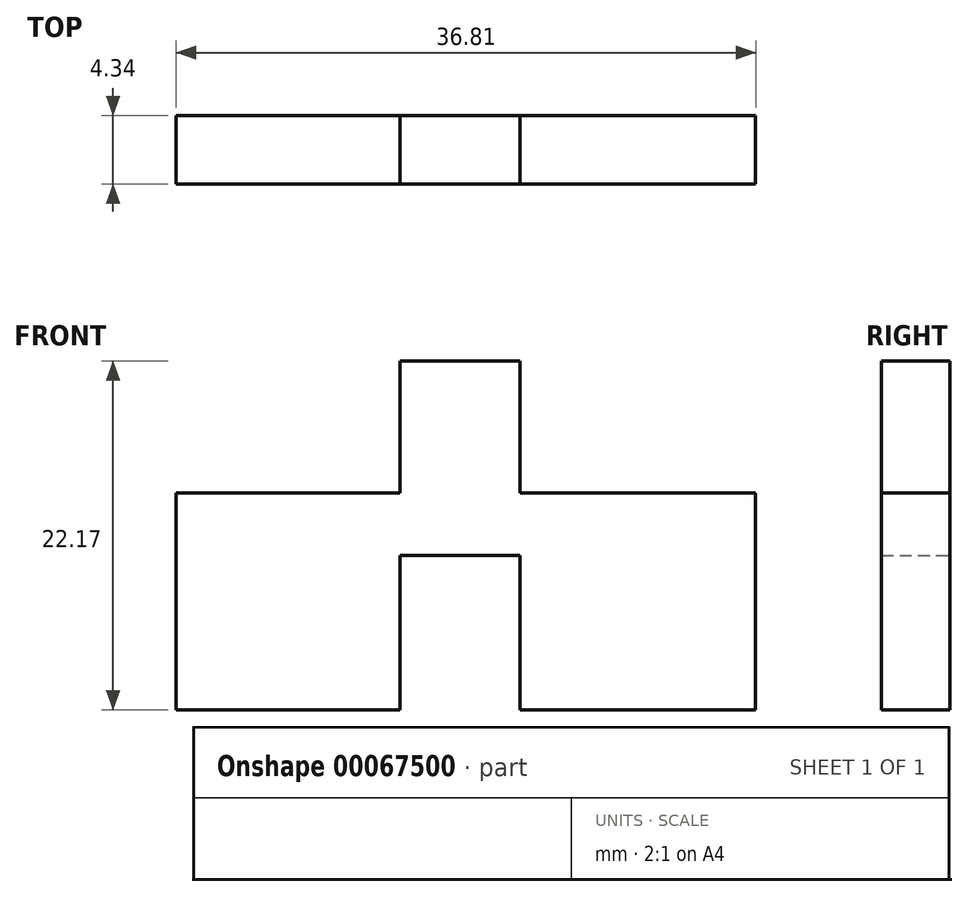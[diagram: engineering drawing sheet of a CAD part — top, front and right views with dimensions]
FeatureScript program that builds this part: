
annotation { "Feature Type Name" : "Feature", "Feature Type Description" : "" }
export const myFeature = defineFeature(function(context is Context, id is Id, definition is map)
    precondition{}
    {
        {
            var Q0;
            Q0=qCreatedBy(makeId("Front.planeOp"),FACE);
            var sketch = newSketch(context, id + "F0", { "sketchPlane" : qUnion([Q0])});
            skLineSegment(sketch, "E0.bottom", {"start": v(-23.81, 14.56) * mm, "end": v(-16.2, 14.56) * mm});
            skLineSegment(sketch, "E0.left", {"start": v(-38.04, 6.17) * mm, "end": v(-38.04, -4.28) * mm});
            skLineSegment(sketch, "E1.left", {"start": v(-23.81, 14.56) * mm, "end": v(-23.81, 6.17) * mm});
            skLineSegment(sketch, "E1.right", {"start": v(-16.2, 14.56) * mm, "end": v(-16.2, 6.17) * mm});
            skPoint(sketch, "E2.orphan", {"position": v(-12.63, 14.56) * mm});
            skPoint(sketch, "E3.orphan", {"position": v(-38.04, 14.56) * mm});
            skPoint(sketch, "E4.orphan", {"position": v(-25.33, 14.56) * mm});
            skPoint(sketch, "E5.end.orphan", {"position": v(-25.33, 0) * mm});
            skLineSegment(sketch, "E6", {"start": v(-38.04, -4.28) * mm, "end": v(-38.04, -7.61) * mm});
            skLineSegment(sketch, "E7.MirrorCS", {"start": v(-1.23, -4.28) * mm, "end": v(-1.23, -7.61) * mm});
            skPoint(sketch, "E8.end.orphan", {"position": v(-30.22, -0.18) * mm});
            skPoint(sketch, "E9.end.orphan", {"position": v(-30.22, -3.5) * mm});
            skLineSegment(sketch, "E10", {"start": v(-38.04, -7.61) * mm, "end": v(-23.81, -7.61) * mm});
            skLineSegment(sketch, "E11", {"start": v(-1.23, 6.17) * mm, "end": v(-1.23, -4.28) * mm});
            skLineSegment(sketch, "E12", {"start": v(-38.04, 6.17) * mm, "end": v(-23.81, 6.17) * mm});
            skPoint(sketch, "E13", {"position": v(-19.64, 6.17) * mm});
            skPoint(sketch, "E14", {"position": v(-20, 14.56) * mm});
            skLineSegment(sketch, "E15.trimOffspring", {"start": v(-16.2, 6.17) * mm, "end": v(-1.23, 6.17) * mm});
            skPoint(sketch, "E16", {"position": v(-19.64, -7.61) * mm});
            skLineSegment(sketch, "E17", {"start": v(-23.81, -7.61) * mm, "end": v(-23.81, 2.2) * mm});
            skLineSegment(sketch, "E18", {"start": v(-16.2, 2.2) * mm, "end": v(-16.2, -7.61) * mm});
            skPoint(sketch, "E19.start.orphan", {"position": v(-23.17, 2.2) * mm});
            skLineSegment(sketch, "E20.trimOffspring", {"start": v(-16.2, -7.61) * mm, "end": v(-1.23, -7.61) * mm});
            skLineSegment(sketch, "E21", {"start": v(-23.81, 2.2) * mm, "end": v(-16.2, 2.2) * mm});
            skPoint(sketch, "E22.orphan", {"position": v(-16.2, 5.7) * mm});
            skSolve(sketch);
        }
        {
            var Q0;
            Q0 = qSketchRegion(id + "F0", true);
            extrude(context, id + "F1", {"entities" : qUnion([Q0]), "depth" : 4.34 * mm});
        }
    });
